# Revit family: Bathtub-Freestanding-DXV-St_George-D62747004_Series
name_source: partatom
category: Plumbing Fixtures
revit_build: Autodesk Revit 2014 (Build: 20130308_1515(x64)
units: mm (PartAtom-declared; Revit-internal decimal feet)

## types (2) — shared parameters
Assembly Code = D2010510
CW Connection = No
Default Elevation = 0"
Description = St. George Freestanding Soaking Tub With Deck
HW Connection = No
Height = 23 1/2"
Installation Type = Freestanding
Length = 35 1/2"
Manufacturer = DXV
Price = Prices may vary. Please consult Manufacturer Representative for most up-to-date price list.
Product Documentation Link = https://dxv01.blob.core.windows.net
Product Page URL = https://www.dxv.com
URL = https://www.dxv.com
Vent Connection = No
WFU = 4
Waste Connection = Yes
Waste Connection Diameter = 1 1/2"
Waste Connection Radius = 3/4"
Width = 66 1/2"
zero-valued in all types: CWFU, HWFU

## per-type parameters (varying)
| type | Body Material | Material |
| D62747004.415 | Acrylic-DXV-415-Canvas White | Acrylic-DXV-415-Canvas White |
| D62747004.071 | Acrylic-DXV-071-Biscuit | Acrylic-DXV-071-Biscuit |

note: column(s) folded — value = type name in every type: Model

## geometry (parser evidence)
native form markers: Sweep x1
no freeform markers — native parametric forms only
